# Revit family: SURE-BOARD-SERIES200B
name_source: partatom
category: Generic Models
units: mm (PartAtom-declared; Revit-internal decimal feet)

## family parameters
Can host rebar = No
Cut with Voids When Loaded = No
Host = Face
Maintain Annotation Orientation = No
Part Type = Normal
Room Calculation Point = No
Round Connector Dimension = Use Diameter
Shared = No

## types (9) — shared parameters
Default Elevation = 4' - 0"
Product Submittal Link = https://cemcosteel.com
SteelSheetThickness = 0' - 0 1/32"
URL = http://www.cemcosteel.com
Width = 4' - 0"

## per-type parameters (varying)
| type | Assembly Code | Description | Keynote | Manufacturer | Material | Product Info | Wallboard Thickness |
| SureBoard200BI-50 |  | Sure-Board® 200B for Blast/Ballistic is an enhanced version of 200, used in pre-tested assemblies for varying degrees of Blast/Ballistic protection. |  | California  Expanded Metal Lath Products Co. (CEMCO) | 22Ga. Sheet Steel | Sure-Board® Series 200B for Blast and Ballistics | 0' - 0 1/2" |
| SureBoard200BB-50 |  | Sure-Board® 200B for Blast/Ballistic is an enhanced version of 200, used in pre-tested assemblies for varying degrees of Blast/Ballistic protection. |  | California  Expanded Metal Lath Products Co. (CEMCO) | 14Ga. Sheet Steel | Sure-Board® Series 200B for Blast and Ballistics | 0' - 0 1/2" |
| SureBoard200BX-50 |  | Sure-Board® 200B for Blast/Ballistic is an enhanced version of 200, used in pre-tested assemblies for varying degrees of Blast/Ballistic protection. |  | California  Expanded Metal Lath Products Co. (CEMCO) | 14Ga. Sheet Steel | Sure-Board® Series 200B for Blast and Ballistics | 0' - 0 1/2" |
| SureBoard200BI-62 |  | Sure-Board® 200B for Blast/Ballistic is an enhanced version of 200, used in pre-tested assemblies for varying degrees of Blast/Ballistic protection. |  | California  Expanded Metal Lath Products Co. (CEMCO) | 22Ga. Sheet Steel | Sure-Board® Series 200B for Blast and Ballistics | 0' - 0 5/8" |
| SureBoard200BI-75 |  | Sure-Board® 200B for Blast/Ballistic is an enhanced version of 200, used in pre-tested assemblies for varying degrees of Blast/Ballistic protection. |  | California  Expanded Metal Lath Products Co. (CEMCO) | 22Ga. Sheet Steel | Sure-Board® Series 200B for Blast and Ballistics | 0' - 0 3/4" |
| SureBoard200BB-62 | B1010220 | Sure-Board® 200B for Blast/Ballistic | 054000 | California  Expanded Metal Lath Products Co. | 14Ga. Sheet Steel | Sure-Board® Series 200B for Blast and Ballistic | 0' - 0 5/8" |
| SureBoard200BB-75 |  | Sure-Board® 200B for Blast/Ballistic is an enhanced version of 200, used in pre-tested assemblies for varying degrees of Blast/Ballistic protection. |  | California  Expanded Metal Lath Products Co. (CEMCO) | 14Ga. Sheet Steel | Sure-Board® Series 200B for Blast and Ballistics | 0' - 0 3/4" |
| SureBoard200BX-62 |  | Sure-Board® 200B for Blast/Ballistic is an enhanced version of 200, used in pre-tested assemblies for varying degrees of Blast/Ballistic protection. |  | California  Expanded Metal Lath Products Co. (CEMCO) | 14Ga. Sheet Steel | Sure-Board® Series 200B for Blast and Ballistics | 0' - 0 5/8" |
| SureBoard200BX-75 |  | Sure-Board® 200B for Blast/Ballistic is an enhanced version of 200, used in pre-tested assemblies for varying degrees of Blast/Ballistic protection. |  | California  Expanded Metal Lath Products Co. (CEMCO) | 14Ga. Sheet Steel | Sure-Board® Series 200B for Blast and Ballistics | 0' - 0 3/4" |

## geometry (parser evidence)
native form markers: Sweep x1
no freeform markers — native parametric forms only
